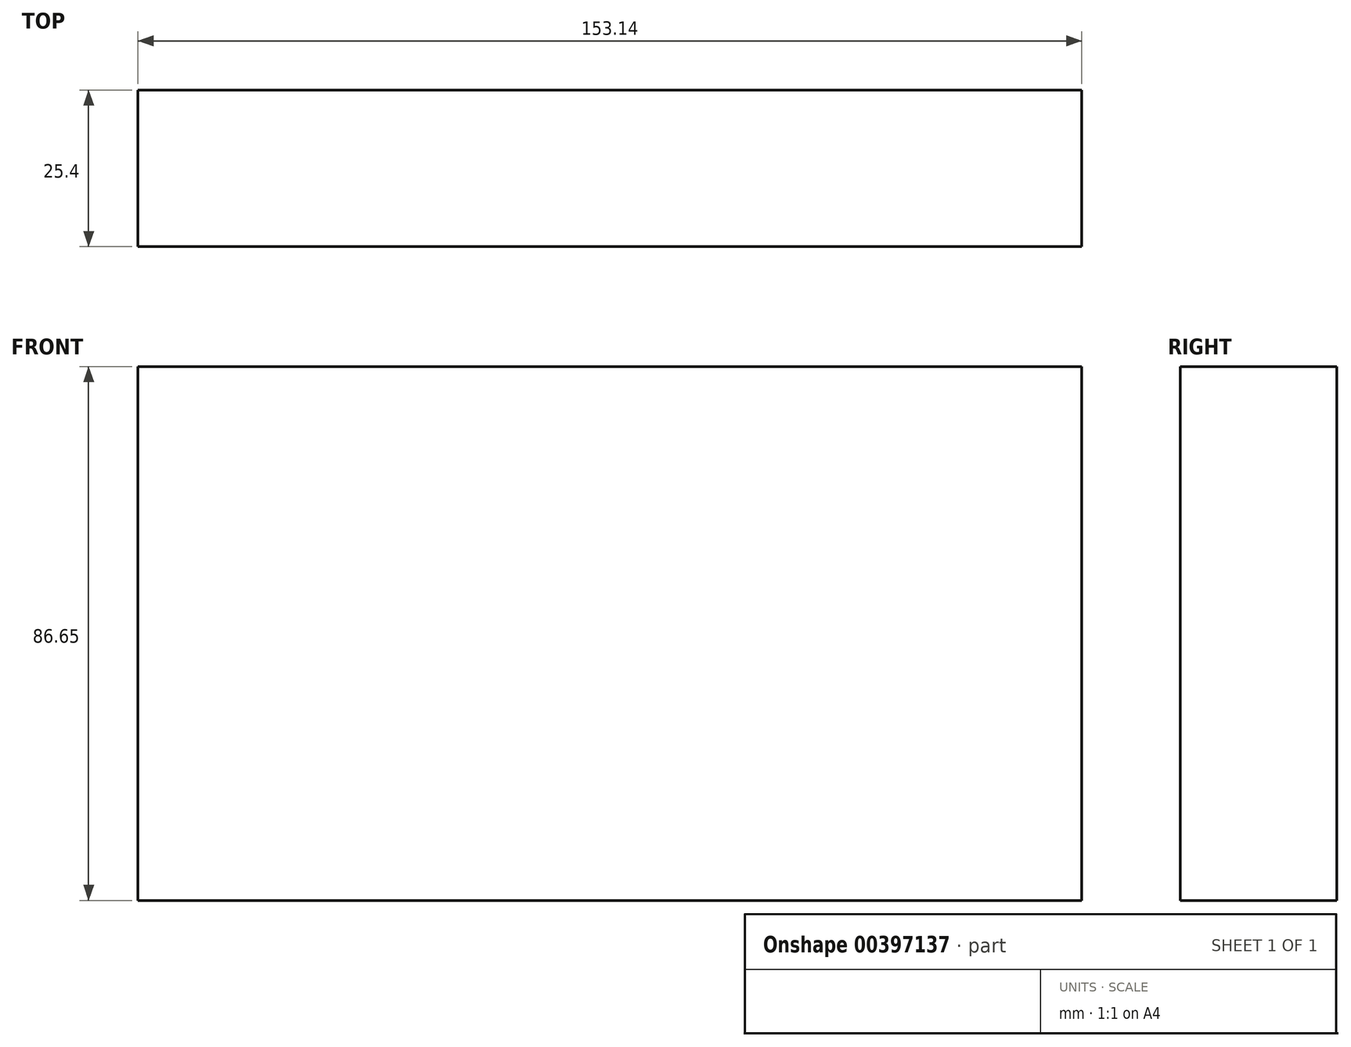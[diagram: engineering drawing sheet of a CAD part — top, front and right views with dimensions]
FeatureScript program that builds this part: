
annotation { "Feature Type Name" : "Feature", "Feature Type Description" : "" }
export const myFeature = defineFeature(function(context is Context, id is Id, definition is map)
    precondition{}
    {
        {
            var Q0;
            Q0=qCreatedBy(makeId("Front.planeOp"),FACE);
            var sketch = newSketch(context, id + "F0", { "sketchPlane" : qUnion([Q0])});
            skLineSegment(sketch, "E0.bottom", {"start": v(0, 0) * mm, "end": v(-153.14, 0) * mm});
            skLineSegment(sketch, "E0.top", {"start": v(0, 86.65) * mm, "end": v(-153.14, 86.65) * mm});
            skLineSegment(sketch, "E0.left", {"start": v(0, 0) * mm, "end": v(0, 86.65) * mm});
            skLineSegment(sketch, "E0.right", {"start": v(-153.14, 0) * mm, "end": v(-153.14, 86.65) * mm});
            skSolve(sketch);
        }
        {
            var Q0;
            Q0=makeQuery(id+"F0.imprint","IMPRINT",FACE,{"disambiguationData":[TD([[makeQuery(id+"F0.imprint","IMPRINT",EDGE,{"derivedFrom":sQuery(id+"F0.wireOp",EDGE,"E0.bottom")}),-1.0]])]});
            extrude(context, id + "F1", {"entities" : qUnion([Q0]), "depth" : 25.4 * mm});
        }
    });
